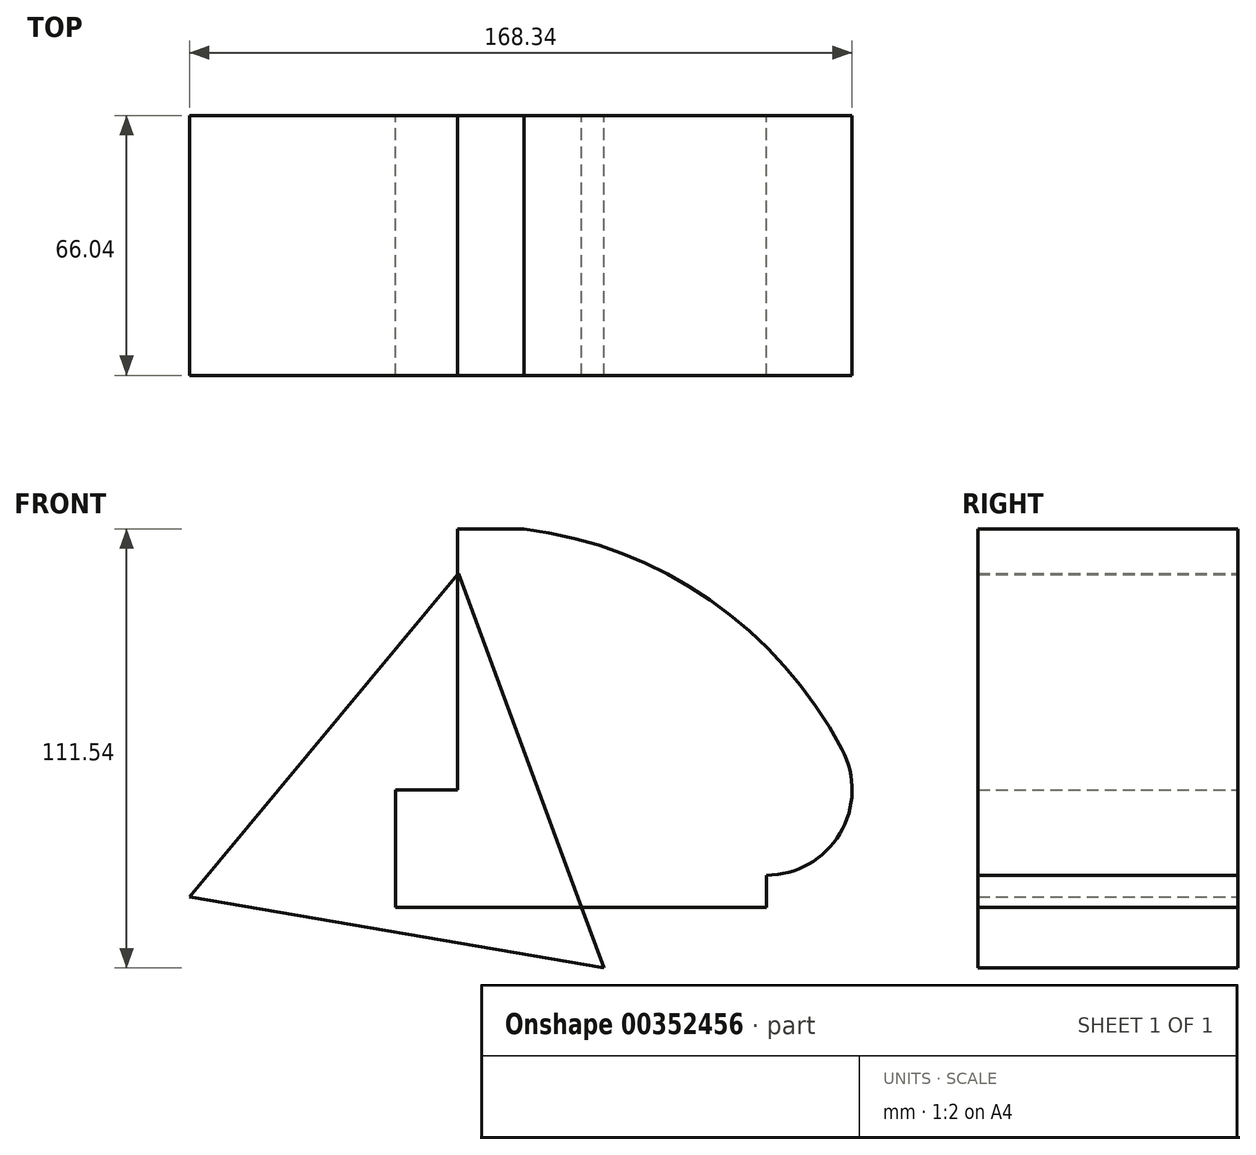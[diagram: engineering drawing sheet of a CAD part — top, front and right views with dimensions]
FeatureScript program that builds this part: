
annotation { "Feature Type Name" : "Feature", "Feature Type Description" : "" }
export const myFeature = defineFeature(function(context is Context, id is Id, definition is map)
    precondition{}
    {
        {
            var Q0;
            Q0=qCreatedBy(makeId("Front.planeOp"),FACE);
            var sketch = newSketch(context, id + "F0", { "sketchPlane" : qUnion([Q0])});
            skLineSegment(sketch, "E0.bottom", {"start": v(-83.55, 15.45) * mm, "end": v(10.73, 15.45) * mm});
            skLineSegment(sketch, "E0.top", {"start": v(-83.55, -14.44) * mm, "end": v(10.73, -14.44) * mm});
            skLineSegment(sketch, "E0.left", {"start": v(-83.55, 15.45) * mm, "end": v(-83.55, -14.44) * mm});
            skLineSegment(sketch, "E0.right", {"start": v(10.73, 15.45) * mm, "end": v(10.73, -14.44) * mm});
            skCircle(sketch, "E1", {"center": v(10.73, 15.45) * mm, "radius": 21.72 * mm});
            skLineSegment(sketch, "E2.bottom", {"start": v(-67.84, 15.45) * mm, "end": v(-50.9, 15.45) * mm});
            skLineSegment(sketch, "E2.top", {"start": v(-67.84, 81.7) * mm, "end": v(-50.9, 81.7) * mm});
            skLineSegment(sketch, "E2.left", {"start": v(-67.84, 15.45) * mm, "end": v(-67.84, 81.7) * mm});
            skLineSegment(sketch, "E2.right", {"start": v(-50.9, 15.45) * mm, "end": v(-50.9, 81.7) * mm});
            skArc(sketch, "E3", {"start": v(30.1, 25.28) * mm, "mid": v(-3.43, 63.5) * mm, "end": v(-50.9, 81.7) * mm});
            skCircle(sketch, "E4.cCircle", {"center": v(-78, 9.6) * mm, "radius": 30.85 * mm, "construction": true});
            skLineSegment(sketch, "E4.0", {"start": v(-135.89, -11.78) * mm, "end": v(-67.58, 70.41) * mm});
            skLineSegment(sketch, "E4.1", {"start": v(-67.58, 70.41) * mm, "end": v(-30.56, -29.84) * mm});
            skLineSegment(sketch, "E4.2", {"start": v(-30.56, -29.84) * mm, "end": v(-135.89, -11.78) * mm});
            skPoint(sketch, "E4.0.midPoint", {"position": v(-101.73, 29.32) * mm});
            skSolve(sketch);
        }
        {
            var Q0;
            {var subQ0=sQuery(id+"F0.wireOp",EDGE,"E0.left");Q0=makeQuery(id+"F0.imprint","IMPRINT",FACE,{"disambiguationData":[TD([[makeQuery(id+"F0.imprint","IMPRINT",EDGE,{"derivedFrom":subQ0}),-1.0]])]});}
            var Q1;
            {var subQ3=sQuery(id+"F0.wireOp",EDGE,"E4.1");var subQ7=sQuery(id+"F0.wireOp",EDGE,"E0.bottom");var subQ9=makeQuery(id+"F0.imprint","INTERSECT",VERTEX,{"derivedFrom":[subQ7,subQ3]});Q1=makeQuery(id+"F0.imprint","IMPRINT",FACE,{"disambiguationData":[TD([[makeQuery(id+"F0.imprint","IMPRINT",EDGE,{"disambiguationData":[TD([[subQ9,-1.0]])],"derivedFrom":subQ7}),1.0]])]});}
            var Q2;
            {var subQ0=sQuery(id+"F0.wireOp",EDGE,"E3");var subQ1=sQuery(id+"F0.wireOp",EDGE,"E1");var subQ2=makeQuery(id+"F0.imprint","INTERSECT",VERTEX,{"disambiguationData":[OD(0.0)],"derivedFrom":[subQ1,subQ0]});Q2=makeQuery(id+"F0.imprint","IMPRINT",FACE,{"disambiguationData":[TD([[makeQuery(id+"F0.imprint","IMPRINT",EDGE,{"disambiguationData":[TD([[subQ2,-1.0]])],"derivedFrom":subQ1}),1.0]])]});}
            var Q3;
            {var subQ6=sQuery(id+"F0.wireOp",EDGE,"E2.top");Q3=makeQuery(id+"F0.imprint","IMPRINT",FACE,{"disambiguationData":[TD([[makeQuery(id+"F0.imprint","IMPRINT",EDGE,{"derivedFrom":subQ6}),-1.0]])]});}
            var Q4;
            {var subQ0=sQuery(id+"F0.wireOp",EDGE,"E0.right");var subQ1=sQuery(id+"F0.wireOp",EDGE,"E0.bottom");var subQ2=makeQuery(id+"F0.imprint","INTERSECT",VERTEX,{"derivedFrom":[subQ1,subQ0]});Q4=makeQuery(id+"F0.imprint","IMPRINT",FACE,{"disambiguationData":[TD([[makeQuery(id+"F0.imprint","IMPRINT",EDGE,{"disambiguationData":[TD([[subQ2,1.0]])],"derivedFrom":subQ1}),-1.0]])]});}
            var Q5;
            {var subQ3=sQuery(id+"F0.wireOp",EDGE,"E0.bottom");var subQ6=sQuery(id+"F0.wireOp",EDGE,"E0.right");var subQ8=makeQuery(id+"F0.imprint","INTERSECT",VERTEX,{"derivedFrom":[subQ3,subQ6]});Q5=makeQuery(id+"F0.imprint","IMPRINT",FACE,{"disambiguationData":[TD([[makeQuery(id+"F0.imprint","IMPRINT",EDGE,{"disambiguationData":[TD([[subQ8,1.0]])],"derivedFrom":subQ3}),1.0]])]});}
            var Q6;
            {var subQ3=sQuery(id+"F0.wireOp",EDGE,"E0.bottom");var subQ7=sQuery(id+"F0.wireOp",EDGE,"E4.1");var subQ9=makeQuery(id+"F0.imprint","INTERSECT",VERTEX,{"derivedFrom":[subQ3,subQ7]});Q6=makeQuery(id+"F0.imprint","IMPRINT",FACE,{"disambiguationData":[TD([[makeQuery(id+"F0.imprint","IMPRINT",EDGE,{"disambiguationData":[TD([[subQ9,-1.0]])],"derivedFrom":subQ3}),-1.0]])]});}
            extrude(context, id + "F1", {"entities" : qUnion([Q0, Q1, Q2, Q3, Q4, Q5, Q6]), "depth" : 66.04 * mm});
        }
    });
